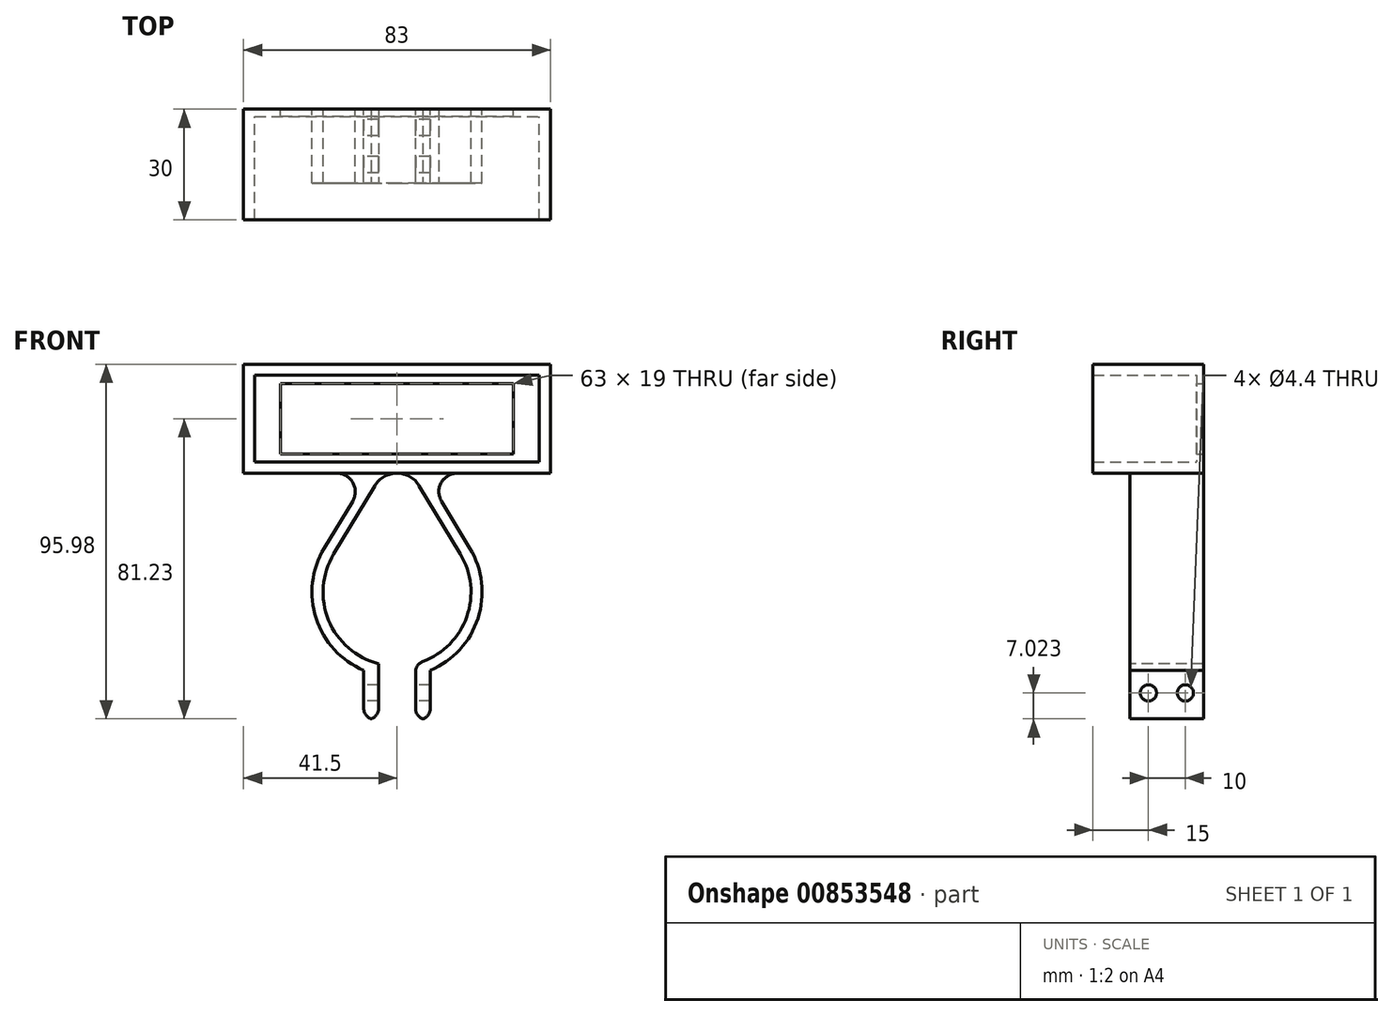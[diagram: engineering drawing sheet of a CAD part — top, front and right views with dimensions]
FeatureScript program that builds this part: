
annotation { "Feature Type Name" : "Feature", "Feature Type Description" : "" }
export const myFeature = defineFeature(function(context is Context, id is Id, definition is map)
    precondition{}
    {
        {
            var Q0;
            Q0=qCreatedBy(makeId("Front.planeOp"),FACE);
            var sketch = newSketch(context, id + "F0", { "sketchPlane" : qUnion([Q0])});
            skArc(sketch, "E0", {"start": v(-17.13, 10.32) * mm, "mid": v(0, -20) * mm, "end": v(17.13, 10.32) * mm});
            skLineSegment(sketch, "E1", {"start": v(-6, 28.81) * mm, "end": v(-17.13, 10.32) * mm});
            skLineSegment(sketch, "E2", {"start": v(-17.13, 10.32) * mm, "end": v(17.13, 10.32) * mm, "construction": true});
            skLineSegment(sketch, "E3", {"start": v(17.13, 10.32) * mm, "end": v(6, 28.81) * mm});
            skArc(sketch, "E4.filletArc", {"start": v(6, 28.81) * mm, "mid": v(0, 32.2) * mm, "end": v(-6, 28.81) * mm});
            skLineSegment(sketch, "E5.0", {"start": v(-8.57, 30.36) * mm, "end": v(-19.7, 11.87) * mm});
            skArc(sketch, "E5.1", {"start": v(8.57, 30.36) * mm, "mid": v(0, 35.2) * mm, "end": v(-8.57, 30.36) * mm});
            skLineSegment(sketch, "E5.2", {"start": v(19.7, 11.87) * mm, "end": v(8.57, 30.36) * mm});
            skArc(sketch, "E5.3", {"start": v(-19.7, 11.87) * mm, "mid": v(0, -23) * mm, "end": v(19.7, 11.87) * mm});
            skPoint(sketch, "E6", {"position": v(0, 32.2) * mm});
            skPoint(sketch, "E6.positionSnap0", {"position": v(0, 32.2) * mm});
            skPoint(sketch, "E7", {"position": v(0, -20) * mm});
            skSolve(sketch);
        }
        {
            var Q0;
            Q0=qSketchRegion(id+"F0",true);
            extrude(context, id + "F1", {"entities" : qUnion([Q0]), "depth" : 20 * mm, "offsetDistance" : 25 * mm});
        }
        {
            var Q0;
            Q0=makeQuery(id+"F1.opExtrude","CAP_FACE",FACE,{"disambiguationData":[OSD([sQuery(id+"F0.wireOp",EDGE,"E0"),sQuery(id+"F0.wireOp",EDGE,"E1"),sQuery(id+"F0.wireOp",EDGE,"E3"),sQuery(id+"F0.wireOp",EDGE,"E4.filletArc"),sQuery(id+"F0.wireOp",EDGE,"9ccc6c94-7c4e-4f0d-8316-c73e20db5738.0"),sQuery(id+"F0.wireOp",EDGE,"6d5136d6-ce14-4da0-b8ac-75ae21cba83e.0"),sQuery(id+"F0.wireOp",EDGE,"d5c29eba-b5d8-48bc-9b3f-04421df860a7.0"),sQuery(id+"F0.wireOp",EDGE,"62930ee1-95c3-4c51-ae63-bd586465ffb3.0")])],"isStart":false});
            var sketch = newSketch(context, id + "F2", { "sketchPlane" : qUnion([Q0])});
            skLineSegment(sketch, "E8.bottom", {"start": v(-5, -19) * mm, "end": v(5, -19) * mm});
            skLineSegment(sketch, "E8.top", {"start": v(-5, -24) * mm, "end": v(5, -24) * mm});
            skLineSegment(sketch, "E8.left", {"start": v(-5, -19) * mm, "end": v(-5, -24) * mm});
            skLineSegment(sketch, "E8.right", {"start": v(5, -19) * mm, "end": v(5, -24) * mm});
            skSolve(sketch);
        }
        {
            var Q0;
            {var subQ0=sQuery(id+"F2.wireOp",EDGE,"E8.left");var subQ1=makeQuery(id+"F1.opExtrude","CAP_EDGE",EDGE,{"disambiguationData":[OSD([sQuery(id+"F0.wireOp",EDGE,"E5.3")])],"isStart":false});var subQ2=makeQuery(id+"F2.imprint","INTERSECT",VERTEX,{"derivedFrom":[subQ1,subQ0]});Q0=makeQuery(id+"F2.imprint","IMPRINT",FACE,{"disambiguationData":[TD([[makeQuery(id+"F2.imprint","IMPRINT",EDGE,{"disambiguationData":[TD([[subQ2,1.0]])],"derivedFrom":subQ0}),1.0]])]});}
            extrude(context, id + "F3", {"entities" : qUnion([Q0]), "operationType" : NewBodyOperationType.REMOVE, "endBound" : BoundingType.THROUGH_ALL, "oppositeDirection" : true, "depth" : 25 * mm, "offsetDistance" : 25 * mm});
        }
        {
            var Q0;
            Q0=qCreatedBy(makeId("Front.planeOp"),FACE);
            var sketch = newSketch(context, id + "F4", { "sketchPlane" : qUnion([Q0])});
            skLineSegment(sketch, "E9", {"start": v(-5, -22.45) * mm, "end": v(-5, -34.45) * mm});
            skLineSegment(sketch, "E10", {"start": v(-5, -34.45) * mm, "end": v(-9, -34.45) * mm});
            skLineSegment(sketch, "E11", {"start": v(-9, -34.45) * mm, "end": v(-9, -21.17) * mm});
            skLineSegment(sketch, "E12", {"start": v(-9, -21.17) * mm, "end": v(-5, -22.45) * mm});
            skLineSegment(sketch, "E13.MirrorCS", {"start": v(9, -34.45) * mm, "end": v(9, -21.17) * mm});
            skLineSegment(sketch, "E14.MirrorCS", {"start": v(9, -21.17) * mm, "end": v(5, -22.45) * mm});
            skLineSegment(sketch, "E15.MirrorCS", {"start": v(5, -34.45) * mm, "end": v(9, -34.45) * mm});
            skLineSegment(sketch, "E16.MirrorCS", {"start": v(5, -22.45) * mm, "end": v(5, -34.45) * mm});
            skSolve(sketch);
        }
        {
            var Q0;
            Q0 = qSketchRegion(id + "F4", true);
            var Q1;
            Q1=makeQuery(id+"F1.opExtrude","CAP_FACE",FACE,{"disambiguationData":[OSD([sQuery(id+"F0.wireOp",EDGE,"E0"),sQuery(id+"F0.wireOp",EDGE,"E1"),sQuery(id+"F0.wireOp",EDGE,"E3"),sQuery(id+"F0.wireOp",EDGE,"E4.filletArc"),sQuery(id+"F0.wireOp",EDGE,"9ccc6c94-7c4e-4f0d-8316-c73e20db5738.0"),sQuery(id+"F0.wireOp",EDGE,"6d5136d6-ce14-4da0-b8ac-75ae21cba83e.0"),sQuery(id+"F0.wireOp",EDGE,"d5c29eba-b5d8-48bc-9b3f-04421df860a7.0"),sQuery(id+"F0.wireOp",EDGE,"62930ee1-95c3-4c51-ae63-bd586465ffb3.0")])],"isStart":false});
            extrude(context, id + "F5", {"entities" : qUnion([Q0]), "operationType" : NewBodyOperationType.ADD, "endBound" : BoundingType.UP_TO_SURFACE, "depth" : 25 * mm, "endBoundEntityFace" : qUnion([Q1]), "offsetDistance" : 25 * mm});
        }
        {
            var Q0;
            Q0=makeQuery(id+"F3.boolean.opBoolean","COPY",EDGE,{"derivedFrom":makeQuery(id+"F3.opExtrude","SWEPT_EDGE",EDGE,{"disambiguationData":[OSD([sQuery(id+"F0.wireOp",EDGE,"E0"),sQuery(id+"F2.wireOp",EDGE,"E8.bottom"),sQuery(id+"F2.wireOp",EDGE,"E8.left")])]})});
            var Q1;
            Q1=makeQuery(id+"F3.boolean.opBoolean","COPY",EDGE,{"derivedFrom":makeQuery(id+"F3.opExtrude","SWEPT_EDGE",EDGE,{"disambiguationData":[OSD([sQuery(id+"F0.wireOp",EDGE,"E0"),sQuery(id+"F2.wireOp",EDGE,"E8.bottom"),sQuery(id+"F2.wireOp",EDGE,"E8.right")])]})});
            var Q2;
            Q2=makeQuery(id+"F5.opExtrude","SWEPT_EDGE",EDGE,{"disambiguationData":[OSD([sQuery(id+"F4.wireOp",EDGE,"E9"),sQuery(id+"F4.wireOp",EDGE,"E10")])]});
            var Q3;
            Q3=makeQuery(id+"F5.opExtrude","SWEPT_EDGE",EDGE,{"disambiguationData":[OSD([sQuery(id+"F4.wireOp",EDGE,"E15.MirrorCS"),sQuery(id+"F4.wireOp",EDGE,"E16.MirrorCS")])]});
            var Q4;
            Q4=makeQuery(id+"F5.opExtrude","SWEPT_EDGE",EDGE,{"disambiguationData":[OSD([sQuery(id+"F4.wireOp",EDGE,"E13.MirrorCS"),sQuery(id+"F4.wireOp",EDGE,"E15.MirrorCS")])]});
            var Q5;
            Q5=makeQuery(id+"F5.opExtrude","SWEPT_EDGE",EDGE,{"disambiguationData":[OSD([sQuery(id+"F4.wireOp",EDGE,"E10"),sQuery(id+"F4.wireOp",EDGE,"E11")])]});
            var Q6;
            Q6=makeQuery(id+"F5.opExtrude","SWEPT_EDGE",EDGE,{"disambiguationData":[OSD([sQuery(id+"F4.wireOp",EDGE,"E11"),sQuery(id+"F4.wireOp",EDGE,"E12")])]});
            var Q7;
            Q7=makeQuery(id+"F5.opExtrude","SWEPT_EDGE",EDGE,{"disambiguationData":[OSD([sQuery(id+"F4.wireOp",EDGE,"E13.MirrorCS"),sQuery(id+"F4.wireOp",EDGE,"E14.MirrorCS")])]});
            fillet(context, id + "F6", {"entities" : qUnion([Q0, Q1, Q2, Q3, Q4, Q5, Q6, Q7]), "radius" : 3 * mm, "tangentPropagation" : true, "allowEdgeOverflow" : false});
        }
        {
            var Q0;
            Q0=qCreatedBy(makeId("Front.planeOp"),FACE);
            var sketch = newSketch(context, id + "F7", { "sketchPlane" : qUnion([Q0])});
            skLineSegment(sketch, "E17.bottom", {"start": v(38.5, 35.2) * mm, "end": v(-38.5, 35.2) * mm});
            skLineSegment(sketch, "E17.top", {"start": v(38.5, 58.7) * mm, "end": v(-38.5, 58.7) * mm});
            skLineSegment(sketch, "E17.left", {"start": v(38.5, 35.2) * mm, "end": v(38.5, 58.7) * mm});
            skLineSegment(sketch, "E17.right", {"start": v(-38.5, 35.2) * mm, "end": v(-38.5, 58.7) * mm});
            skPoint(sketch, "E17.middle", {"position": v(0, 46.95) * mm});
            skLineSegment(sketch, "E18.bottom", {"start": v(41.5, 32.2) * mm, "end": v(-41.5, 32.2) * mm});
            skLineSegment(sketch, "E18.top", {"start": v(41.5, 61.7) * mm, "end": v(-41.5, 61.7) * mm});
            skLineSegment(sketch, "E18.left", {"start": v(41.5, 32.2) * mm, "end": v(41.5, 61.7) * mm});
            skLineSegment(sketch, "E18.right", {"start": v(-41.5, 32.2) * mm, "end": v(-41.5, 61.7) * mm});
            skSolve(sketch);
        }
        {
            var Q0;
            Q0 = qSketchRegion(id + "F7", true);
            extrude(context, id + "F8", {"entities" : qUnion([Q0]), "operationType" : NewBodyOperationType.ADD, "depth" : 30 * mm, "offsetDistance" : 25 * mm});
        }
        {
            var Q0;
            Q0=makeQuery(id+"F8.boolean.opBoolean","INTERSECT",EDGE,{"disambiguationData":[OD(0.0)],"derivedFrom":[makeQuery(id+"F1.opExtrude","SWEPT_FACE",FACE,{"disambiguationData":[OSD([sQuery(id+"F0.wireOp",EDGE,"E5.1")])]}),makeQuery(id+"F8.opExtrude","SWEPT_FACE",FACE,{"disambiguationData":[OSD([sQuery(id+"F7.wireOp",EDGE,"E18.bottom")])]})]});
            var Q1;
            Q1=makeQuery(id+"F8.boolean.opBoolean","INTERSECT",EDGE,{"disambiguationData":[OD(1.0)],"derivedFrom":[makeQuery(id+"F1.opExtrude","SWEPT_FACE",FACE,{"disambiguationData":[OSD([sQuery(id+"F0.wireOp",EDGE,"E5.1")])]}),makeQuery(id+"F8.opExtrude","SWEPT_FACE",FACE,{"disambiguationData":[OSD([sQuery(id+"F7.wireOp",EDGE,"E18.bottom")])]})]});
            fillet(context, id + "F9", {"entities" : qUnion([Q0, Q1]), "radius" : 5 * mm, "tangentPropagation" : true, "allowEdgeOverflow" : false});
        }
        {
            var Q0;
            Q0=makeQuery(id+"F5.opExtrude","SWEPT_FACE",FACE,{"disambiguationData":[OSD([sQuery(id+"F4.wireOp",EDGE,"E11")])]});
            var sketch = newSketch(context, id + "F10", { "sketchPlane" : qUnion([Q0])});
            skCircle(sketch, "E19", {"center": v(5, -27.26) * mm, "radius": 2.2 * mm});
            skPoint(sketch, "E19.centerSnap0", {"position": v(20, -27.26) * mm});
            skPoint(sketch, "E19.centerSnap1", {"position": v(10, -23.07) * mm});
            skLineSegment(sketch, "E20", {"start": v(10, -23.07) * mm, "end": v(10, -31.45) * mm, "construction": true});
            skCircle(sketch, "E21.MirrorC", {"center": v(15, -27.26) * mm, "radius": 2.2 * mm});
            skSolve(sketch);
        }
        {
            var Q0;
            Q0 = qSketchRegion(id + "F10", true);
            extrude(context, id + "F11", {"entities" : qUnion([Q0]), "operationType" : NewBodyOperationType.REMOVE, "endBound" : BoundingType.THROUGH_ALL, "oppositeDirection" : true, "depth" : 25 * mm, "offsetDistance" : 25 * mm});
        }
        {
            var Q0;
            Q0=qCreatedBy(makeId("Front.planeOp"),FACE);
            var sketch = newSketch(context, id + "F12", { "sketchPlane" : qUnion([Q0])});
            skLineSegment(sketch, "E22.bottom", {"start": v(-38.5, 58.7) * mm, "end": v(38.5, 58.7) * mm});
            skLineSegment(sketch, "E22.top", {"start": v(-38.5, 35.2) * mm, "end": v(38.5, 35.2) * mm});
            skLineSegment(sketch, "E22.left", {"start": v(-38.5, 58.7) * mm, "end": v(-38.5, 35.2) * mm});
            skLineSegment(sketch, "E22.right", {"start": v(38.5, 58.7) * mm, "end": v(38.5, 35.2) * mm});
            skLineSegment(sketch, "E23.bottom", {"start": v(31.5, 37.45) * mm, "end": v(-31.5, 37.45) * mm});
            skLineSegment(sketch, "E23.top", {"start": v(31.5, 56.45) * mm, "end": v(-31.5, 56.45) * mm});
            skLineSegment(sketch, "E23.left", {"start": v(31.5, 37.45) * mm, "end": v(31.5, 56.45) * mm});
            skLineSegment(sketch, "E23.right", {"start": v(-31.5, 37.45) * mm, "end": v(-31.5, 56.45) * mm});
            skPoint(sketch, "E23.middle", {"position": v(0, 46.95) * mm});
            skPoint(sketch, "E24", {"position": v(38.5, 46.95) * mm});
            skSolve(sketch);
        }
        {
            var Q0;
            Q0 = qSketchRegion(id + "F12", true);
            extrude(context, id + "F13", {"entities" : qUnion([Q0]), "operationType" : NewBodyOperationType.ADD, "depth" : 2 * mm, "offsetDistance" : 25 * mm});
        }
    });
